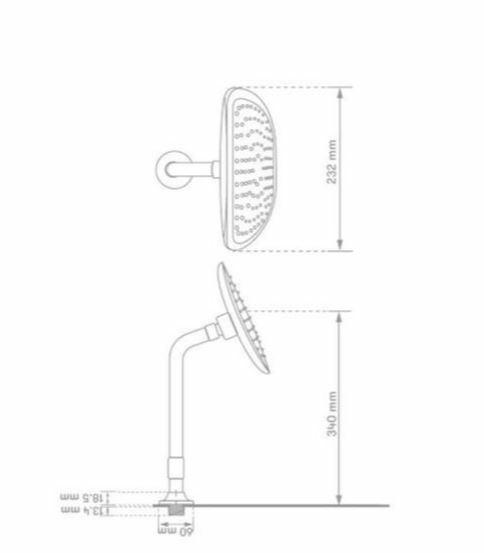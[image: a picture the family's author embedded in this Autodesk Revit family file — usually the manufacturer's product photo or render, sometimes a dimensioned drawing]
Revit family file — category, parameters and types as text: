
# Revit family: 01-0942-11 MEZCLADOR DUCHA 8” CON SALIDA HELVETIA
name_source: partatom
category: Plumbing Fixtures
revit_build: Autodesk Revit 2018 (Build: 20170223_1515(x64)
units: mm (PartAtom-declared; Revit-internal decimal feet)

## family parameters
Cut with Voids When Loaded = No
Host = Face
OmniClass Number = 23.31.11.00
Part Type = Normal
Room Calculation Point = No
Round Connector Dimension = Use Diameter
Shared = No

## types (1)
- 01-0942-11
    Alto = 60 mm  [stored 0.19685 ft]
    Alto- salida tina = 120 mm
    Ancho = 60 mm  [stored 0.19685 ft]
    CW Connection = Yes
    Default Elevation = 0 mm  [stored 0 ft]
    Description = Mezclador ducha
    Distancia entre griferias = 203 mm
    HW Connection = Yes
    Link Ficha Tecnica = http://infotecnica.gricol.com
    Manufacturer = Gricol
    Metal Acero Inoxidable Cromado = Metal Acero Inoxidable Cromado
    Metal Laton Cromado = Metal Laton Cromado
    Mezclador = Mezclador
    Model = 01-0942-11
    Plastico ABS Cromado = Plastico ABS Cromado
    Product Name = MEZCLADOR DUCHA 8” CON SALIDA HELVETIA
    Profundidad = 85 mm  [stored 0.278871 ft]
    Sepacion entre registro y ducha = 400 mm  [stored 1.31234 ft]
    Type Image = <None>
    URL = https://www.gricol.com
    Vent Connection = No
    Waste Connection = No

note: [stored X ft] marks values corroborated as IEEE doubles in the binary element streams (Revit-internal decimal feet)

## geometry (parser evidence)
native form markers: Blend x2, Sweep x25
no freeform markers — native parametric forms only
